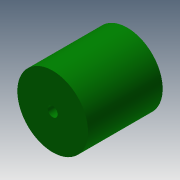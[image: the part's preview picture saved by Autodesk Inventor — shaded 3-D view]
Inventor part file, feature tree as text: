
AUTODESK INVENTOR PART (.ipt)
format: ipt  version: 2013 (Build 170138000, 138)  size: 76,800 bytes
history: native  units: mm
features: extrude x1, sketch x1
ambient origin geometry x8: Origin, YZ Plane, XZ Plane, XY Plane, X Axis, Y Axis, Z Axis, Center Point
bodies: Solid1 (feature_tree)
feature tree (2):
  extrude  "Extrusion1"  Depth=7.0mm
  sketch  "Sketch1"  dims[d0=50.0mm d1=7.0mm d2=52.7mm d3=0.0mm]
